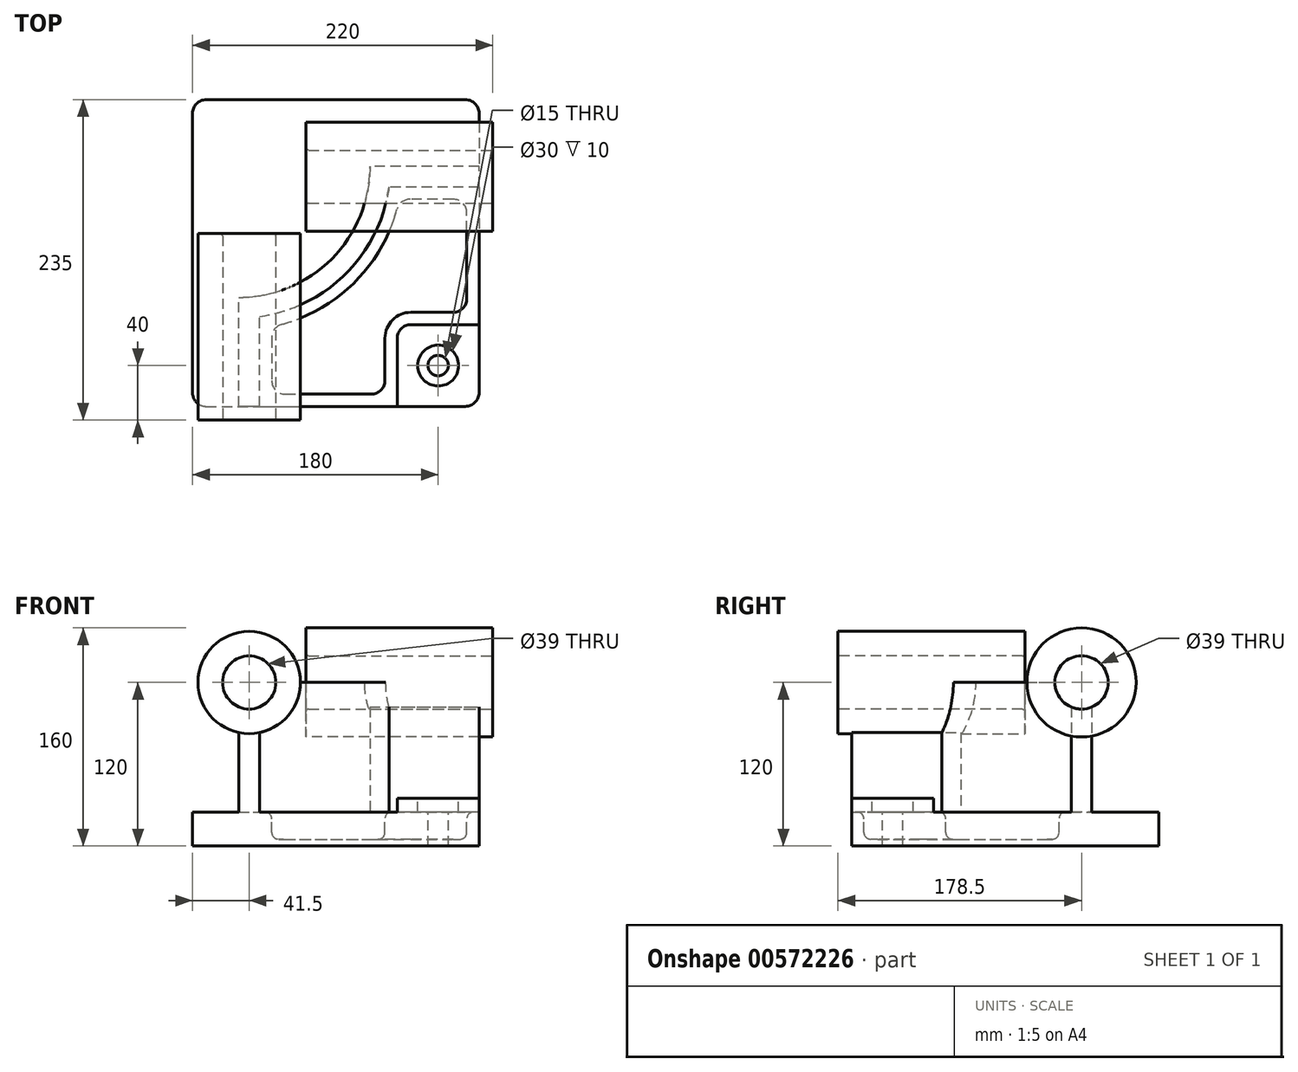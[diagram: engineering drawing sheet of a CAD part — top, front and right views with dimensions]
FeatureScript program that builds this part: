
annotation { "Feature Type Name" : "Feature", "Feature Type Description" : "" }
export const myFeature = defineFeature(function(context is Context, id is Id, definition is map)
    precondition{}
    {
        {
            var Q0;
            Q0=qCreatedBy(makeId("Top.planeOp"),FACE);
            var sketch = newSketch(context, id + "F0", { "sketchPlane" : qUnion([Q0])});
            skLineSegment(sketch, "E0.bottom", {"start": v(-105, 112.5) * mm, "end": v(105, 112.5) * mm});
            skLineSegment(sketch, "E0.top", {"start": v(-105, -112.5) * mm, "end": v(105, -112.5) * mm});
            skLineSegment(sketch, "E0.left", {"start": v(-105, 112.5) * mm, "end": v(-105, -112.5) * mm});
            skLineSegment(sketch, "E0.right", {"start": v(105, 112.5) * mm, "end": v(105, -112.5) * mm});
            skPoint(sketch, "E0.middle", {"position": v(0, 0) * mm});
            skSolve(sketch);
        }
        {
            var Q0;
            Q0=makeQuery(id+"F0.imprint","IMPRINT",FACE,{"disambiguationData":[TD([[makeQuery(id+"F0.imprint","IMPRINT",EDGE,{"derivedFrom":sQuery(id+"F0.wireOp",EDGE,"E0.bottom")}),-1.0]])]});
            extrude(context, id + "F1", {"entities" : qUnion([Q0]), "depth" : 25 * mm});
        }
        {
            var Q0;
            Q0=makeQuery(id+"F1.opExtrude","CAP_FACE",FACE,{"disambiguationData":[OSD([sQuery(id+"F0.wireOp",EDGE,"E0.bottom"),sQuery(id+"F0.wireOp",EDGE,"E0.top"),sQuery(id+"F0.wireOp",EDGE,"E0.left"),sQuery(id+"F0.wireOp",EDGE,"E0.right")])],"isStart":false});
            var sketch = newSketch(context, id + "F2", { "sketchPlane" : qUnion([Q0])});
            skLineSegment(sketch, "E1", {"start": v(-71, -112.5) * mm, "end": v(-71, -32.5) * mm});
            skLineSegment(sketch, "E2", {"start": v(105, 63.5) * mm, "end": v(25, 63.5) * mm});
            skArc(sketch, "E3", {"start": v(-71, -32.5) * mm, "mid": v(-3.11, -4.39) * mm, "end": v(25, 63.5) * mm});
            skLineSegment(sketch, "E4", {"start": v(25, 63.5) * mm, "end": v(-71, 63.5) * mm, "construction": true});
            skLineSegment(sketch, "E5", {"start": v(-71, 63.5) * mm, "end": v(-71, -32.5) * mm, "construction": true});
            skLineSegment(sketch, "E6.0", {"start": v(105, 48.5) * mm, "end": v(38.98, 48.5) * mm});
            skArc(sketch, "E6.1", {"start": v(-56, -46.48) * mm, "mid": v(7.5, -15) * mm, "end": v(38.98, 48.5) * mm});
            skLineSegment(sketch, "E6.2", {"start": v(-56, -112.5) * mm, "end": v(-56, -46.48) * mm});
            skSolve(sketch);
        }
        {
            var Q0;
            {var subQ3=sQuery(id+"F2.wireOp",EDGE,"E1");Q0=makeQuery(id+"F2.imprint","IMPRINT",FACE,{"disambiguationData":[TD([[makeQuery(id+"F2.imprint","IMPRINT",EDGE,{"derivedFrom":subQ3}),-1.0]])]});}
            extrude(context, id + "F3", {"entities" : qUnion([Q0]), "operationType" : NewBodyOperationType.ADD, "depth" : 95 * mm});
        }
        {
            var Q0;
            {var subQ0=sQuery(id+"F0.wireOp",EDGE,"E0.top");Q0=makeQuery(id+"F3.boolean.opBoolean","MERGE",FACE,{"derivedFrom":[makeQuery(id+"F1.opExtrude","SWEPT_FACE",FACE,{"disambiguationData":[OSD([subQ0])]}),makeQuery(id+"F3.opExtrude","SWEPT_FACE",FACE,{"disambiguationData":[OSD([subQ0])]})]});}
            var sketch = newSketch(context, id + "F4", { "sketchPlane" : qUnion([Q0])});
            skCircle(sketch, "E7", {"center": v(-63.5, 120) * mm, "radius": 37.5 * mm});
            skSolve(sketch);
        }
        {
            var Q0;
            {var subQ1=sQuery(id+"F0.wireOp",EDGE,"E0.top");var subQ6=makeQuery(id+"F3.opExtrude","CAP_EDGE",EDGE,{"disambiguationData":[OSD([subQ1])],"isStart":false});Q0=makeQuery(id+"F4.imprint","IMPRINT",FACE,{"disambiguationData":[TD([[makeQuery(id+"F4.imprint","IMPRINT",EDGE,{"derivedFrom":subQ6}),-1.0]])]});}
            var Q1;
            {var subQ1=sQuery(id+"F0.wireOp",EDGE,"E0.top");var subQ6=makeQuery(id+"F3.opExtrude","CAP_EDGE",EDGE,{"disambiguationData":[OSD([subQ1])],"isStart":false});Q1=makeQuery(id+"F4.imprint","IMPRINT",FACE,{"disambiguationData":[TD([[makeQuery(id+"F4.imprint","IMPRINT",EDGE,{"derivedFrom":subQ6}),1.0]])]});}
            var Q2;
            Q2=sQuery(id+"F4.wireOp",EDGE,"E7");
            extrude(context, id + "F5", {"entities" : qUnion([Q0, Q1]), "operationType" : NewBodyOperationType.ADD, "surfaceEntities" : qUnion([Q2]), "depth" : 10 * mm, "hasSecondDirection" : true, "secondDirectionOppositeDirection" : true, "secondDirectionDepth" : 137 * mm - 10 * mm});
        }
        {
            var Q0;
            {var subQ0=sQuery(id+"F0.wireOp",EDGE,"E0.right");Q0=makeQuery(id+"F3.boolean.opBoolean","MERGE",FACE,{"derivedFrom":[makeQuery(id+"F1.opExtrude","SWEPT_FACE",FACE,{"disambiguationData":[OSD([subQ0])]}),makeQuery(id+"F3.opExtrude","SWEPT_FACE",FACE,{"disambiguationData":[OSD([subQ0])]})]});}
            var sketch = newSketch(context, id + "F6", { "sketchPlane" : qUnion([Q0])});
            skCircle(sketch, "E8", {"center": v(56, 120) * mm, "radius": 40 * mm});
            skSolve(sketch);
        }
        {
            var Q0;
            {var subQ1=sQuery(id+"F0.wireOp",EDGE,"E0.right");var subQ6=makeQuery(id+"F3.opExtrude","CAP_EDGE",EDGE,{"disambiguationData":[OSD([subQ1])],"isStart":false});Q0=makeQuery(id+"F6.imprint","IMPRINT",FACE,{"disambiguationData":[TD([[makeQuery(id+"F6.imprint","IMPRINT",EDGE,{"derivedFrom":subQ6}),-1.0]])]});}
            var Q1;
            {var subQ1=sQuery(id+"F0.wireOp",EDGE,"E0.right");var subQ6=makeQuery(id+"F3.opExtrude","CAP_EDGE",EDGE,{"disambiguationData":[OSD([subQ1])],"isStart":false});Q1=makeQuery(id+"F6.imprint","IMPRINT",FACE,{"disambiguationData":[TD([[makeQuery(id+"F6.imprint","IMPRINT",EDGE,{"derivedFrom":subQ6}),1.0]])]});}
            var Q2;
            Q2=sQuery(id+"F6.wireOp",EDGE,"E8");
            extrude(context, id + "F7", {"entities" : qUnion([Q0, Q1]), "surfaceEntities" : qUnion([Q2]), "depth" : 10 * mm, "hasSecondDirection" : true, "secondDirectionOppositeDirection" : true, "secondDirectionDepth" : 127 * mm});
        }
        {
            var Q0;
            {var subQ0=sQuery(id+"F0.wireOp",EDGE,"E0.right");var subQ1=sQuery(id+"F0.wireOp",EDGE,"E0.top");Q0=makeQuery(id+"F3.boolean.opBoolean","SPLIT",FACE,{"disambiguationData":[TD([makeQuery(id+"F3.opExtrude","SWEPT_FACE",FACE,{"disambiguationData":[OSD([sQuery(id+"F2.wireOp",EDGE,"E6.0")])]})])],"derivedFrom":makeQuery(id+"F1.opExtrude","CAP_FACE",FACE,{"disambiguationData":[OSD([sQuery(id+"F0.wireOp",EDGE,"E0.bottom"),subQ1,sQuery(id+"F0.wireOp",EDGE,"E0.left"),subQ0])],"isStart":false})});}
            var sketch = newSketch(context, id + "F8", { "sketchPlane" : qUnion([Q0])});
            skLineSegment(sketch, "E9.bottom", {"start": v(105, -112.5) * mm, "end": v(45, -112.5) * mm});
            skLineSegment(sketch, "E9.top", {"start": v(105, -52.5) * mm, "end": v(45, -52.5) * mm});
            skLineSegment(sketch, "E9.left", {"start": v(105, -112.5) * mm, "end": v(105, -52.5) * mm});
            skLineSegment(sketch, "E9.right", {"start": v(45, -112.5) * mm, "end": v(45, -52.5) * mm});
            skSolve(sketch);
        }
        {
            var Q0;
            Q0=qSketchRegion(id+"F8",true);
            extrude(context, id + "F9", {"entities" : qUnion([Q0]), "operationType" : NewBodyOperationType.ADD, "depth" : 10 * mm});
        }
        {
            var Q0;
            Q0=makeQuery(id+"F9.opExtrude","SWEPT_EDGE",EDGE,{"disambiguationData":[OSD([sQuery(id+"F8.wireOp",EDGE,"E9.top"),sQuery(id+"F8.wireOp",EDGE,"E9.right")])]});
            fillet(context, id + "F10", {"entities" : qUnion([Q0]), "radius" : 10 * mm, "tangentPropagation" : true, "allowEdgeOverflow" : false});
        }
        {
            var Q0;
            {var subQ0=sQuery(id+"F0.wireOp",EDGE,"E0.right");var subQ1=sQuery(id+"F0.wireOp",EDGE,"E0.top");Q0=makeQuery(id+"F3.boolean.opBoolean","SPLIT",FACE,{"disambiguationData":[TD([makeQuery(id+"F3.opExtrude","SWEPT_FACE",FACE,{"disambiguationData":[OSD([sQuery(id+"F2.wireOp",EDGE,"E6.0")])]})])],"derivedFrom":makeQuery(id+"F1.opExtrude","CAP_FACE",FACE,{"disambiguationData":[OSD([sQuery(id+"F0.wireOp",EDGE,"E0.bottom"),subQ1,sQuery(id+"F0.wireOp",EDGE,"E0.left"),subQ0])],"isStart":false})});}
            var sketch = newSketch(context, id + "F11", { "sketchPlane" : qUnion([Q0])});
            skLineSegment(sketch, "E10.0", {"start": v(-47, -54.08) * mm, "end": v(-47, -103.5) * mm});
            skArc(sketch, "E10.1", {"start": v(46.58, 39.5) * mm, "mid": v(13.86, -21.36) * mm, "end": v(-47, -54.08) * mm});
            skLineSegment(sketch, "E10.2", {"start": v(-47, -103.5) * mm, "end": v(36, -103.5) * mm});
            skLineSegment(sketch, "E10.3", {"start": v(96, 39.5) * mm, "end": v(46.58, 39.5) * mm});
            skLineSegment(sketch, "E10.4", {"start": v(36, -103.5) * mm, "end": v(36, -62.5) * mm});
            skArc(sketch, "E10.5", {"start": v(36, -62.5) * mm, "mid": v(41.56, -49.06) * mm, "end": v(55, -43.5) * mm});
            skLineSegment(sketch, "E10.6", {"start": v(55, -43.5) * mm, "end": v(96, -43.5) * mm});
            skLineSegment(sketch, "E10.7", {"start": v(96, -43.5) * mm, "end": v(96, 39.5) * mm});
            skSolve(sketch);
        }
        {
            var Q0;
            Q0=makeQuery(id+"F11.imprint","IMPRINT",FACE,{"disambiguationData":[TD([[makeQuery(id+"F11.imprint","IMPRINT",EDGE,{"derivedFrom":sQuery(id+"F11.wireOp",EDGE,"E10.0")}),1.0]])]});
            extrude(context, id + "F12", {"entities" : qUnion([Q0]), "operationType" : NewBodyOperationType.REMOVE, "oppositeDirection" : true, "depth" : 20 * mm});
        }
        {
            var Q0;
            Q0=makeQuery(id+"F9.opExtrude","CAP_FACE",FACE,{"disambiguationData":[OSD([sQuery(id+"F8.wireOp",EDGE,"E9.bottom"),sQuery(id+"F8.wireOp",EDGE,"E9.top"),sQuery(id+"F8.wireOp",EDGE,"E9.left"),sQuery(id+"F8.wireOp",EDGE,"E9.right")])],"isStart":false});
            var sketch = newSketch(context, id + "F13", { "sketchPlane" : qUnion([Q0])});
            skCircle(sketch, "E11", {"center": v(75, -82.5) * mm, "radius": 15 * mm});
            skSolve(sketch);
        }
        {
            var Q0;
            Q0=sQuery(id+"F13.wireOp",VERTEX,"E11.center");
            var Q1;
            Q1=makeQuery(id+"F1.opExtrude","SWEPT_BODY",BODY,{"disambiguationData":[OSD([sQuery(id+"F0.wireOp",EDGE,"E0.bottom"),sQuery(id+"F0.wireOp",EDGE,"E0.top"),sQuery(id+"F0.wireOp",EDGE,"E0.left"),sQuery(id+"F0.wireOp",EDGE,"E0.right")])]});
            hole(context, id + "F14", {"style" : HoleStyle.C_BORE, "endStyle" : HoleEndStyle.THROUGH, "holeDiameter" : 15 * mm, "cBoreDiameter" : 30 * mm, "cBoreDepth" : 10 * mm, "isTappedThrough" : true, "tappedDepth" : 12.7 * mm, "tapClearance" : 3, "locations" : qUnion([Q0]), "scope" : qUnion([Q1])});
        }
        {
            var Q0;
            Q0=makeQuery(id+"F12.boolean.opBoolean","COPY",EDGE,{"derivedFrom":makeQuery(id+"F12.opExtrude","SWEPT_EDGE",EDGE,{"disambiguationData":[OSD([sQuery(id+"F11.wireOp",EDGE,"E10.0"),sQuery(id+"F11.wireOp",EDGE,"E10.1")])]})});
            var Q1;
            Q1=makeQuery(id+"F12.boolean.opBoolean","COPY",EDGE,{"derivedFrom":makeQuery(id+"F12.opExtrude","SWEPT_EDGE",EDGE,{"disambiguationData":[OSD([sQuery(id+"F11.wireOp",EDGE,"E10.1"),sQuery(id+"F11.wireOp",EDGE,"E10.3")])]})});
            var Q2;
            Q2=makeQuery(id+"F12.boolean.opBoolean","COPY",EDGE,{"derivedFrom":makeQuery(id+"F12.opExtrude","SWEPT_EDGE",EDGE,{"disambiguationData":[OSD([sQuery(id+"F11.wireOp",EDGE,"E10.3"),sQuery(id+"F11.wireOp",EDGE,"E10.7")])]})});
            var Q3;
            Q3=makeQuery(id+"F12.boolean.opBoolean","COPY",EDGE,{"derivedFrom":makeQuery(id+"F12.opExtrude","SWEPT_EDGE",EDGE,{"disambiguationData":[OSD([sQuery(id+"F11.wireOp",EDGE,"E10.6"),sQuery(id+"F11.wireOp",EDGE,"E10.7")])]})});
            var Q4;
            Q4=makeQuery(id+"F12.boolean.opBoolean","COPY",EDGE,{"derivedFrom":makeQuery(id+"F12.opExtrude","SWEPT_EDGE",EDGE,{"disambiguationData":[OSD([sQuery(id+"F11.wireOp",EDGE,"E10.2"),sQuery(id+"F11.wireOp",EDGE,"E10.4")])]})});
            var Q5;
            Q5=makeQuery(id+"F12.boolean.opBoolean","COPY",EDGE,{"derivedFrom":makeQuery(id+"F12.opExtrude","SWEPT_EDGE",EDGE,{"disambiguationData":[OSD([sQuery(id+"F11.wireOp",EDGE,"E10.0"),sQuery(id+"F11.wireOp",EDGE,"E10.2")])]})});
            fillet(context, id + "F15", {"entities" : qUnion([Q0, Q1, Q2, Q3, Q4, Q5]), "radius" : 10 * mm, "tangentPropagation" : true, "allowEdgeOverflow" : false});
        }
        {
            var Q0;
            Q0=makeQuery(id+"F5.opExtrude","CAP_FACE",FACE,{"disambiguationData":[OSD([sQuery(id+"F4.wireOp",EDGE,"E7")])],"isStart":false});
            var sketch = newSketch(context, id + "F16", { "sketchPlane" : qUnion([Q0])});
            skCircle(sketch, "E12", {"center": v(-63.5, 120) * mm, "radius": 19.5 * mm});
            skSolve(sketch);
        }
        {
            var Q0;
            Q0=makeQuery(id+"F7.opExtrude","CAP_FACE",FACE,{"disambiguationData":[OSD([sQuery(id+"F6.wireOp",EDGE,"E8")])],"isStart":false});
            var sketch = newSketch(context, id + "F17", { "sketchPlane" : qUnion([Q0])});
            skCircle(sketch, "E13", {"center": v(56, 120) * mm, "radius": 19.5 * mm});
            skSolve(sketch);
        }
        {
            var Q0;
            Q0=qSketchRegion(id+"F16",true);
            extrude(context, id + "F18", {"entities" : qUnion([Q0]), "operationType" : NewBodyOperationType.REMOVE, "endBound" : BoundingType.THROUGH_ALL, "oppositeDirection" : true, "depth" : 25.4 * mm});
        }
        {
            var Q0;
            Q0=makeQuery(id+"F17.imprint","IMPRINT",FACE,{"disambiguationData":[TD([[makeQuery(id+"F17.imprint","IMPRINT",EDGE,{"derivedFrom":sQuery(id+"F17.wireOp",EDGE,"E13")}),1.0]])]});
            extrude(context, id + "F19", {"entities" : qUnion([Q0]), "operationType" : NewBodyOperationType.REMOVE, "endBound" : BoundingType.THROUGH_ALL, "oppositeDirection" : true, "depth" : 25.4 * mm});
        }
        {
            var Q0;
            Q0=makeQuery(id+"F18.boolean.opBoolean","COPY",EDGE,{"derivedFrom":makeQuery(id+"F18.opExtrude","CAP_EDGE",EDGE,{"disambiguationData":[OSD([sQuery(id+"F16.wireOp",EDGE,"E12")])],"isStart":true})});
            var Q1;
            Q1=makeQuery(id+"F19.boolean.opBoolean","COPY",EDGE,{"derivedFrom":makeQuery(id+"F19.opExtrude","CAP_EDGE",EDGE,{"disambiguationData":[OSD([sQuery(id+"F17.wireOp",EDGE,"E13")])],"isStart":true})});
            var Q2;
            Q2=makeQuery(id+"F19.boolean.opBoolean","INTERSECT",EDGE,{"derivedFrom":[makeQuery(id+"F7.opExtrude","CAP_FACE",FACE,{"disambiguationData":[OSD([sQuery(id+"F6.wireOp",EDGE,"E8")])],"isStart":true}),makeQuery(id+"F19.opExtrude","SWEPT_FACE",FACE,{"disambiguationData":[OSD([sQuery(id+"F17.wireOp",EDGE,"E13")])]})]});
            var Q3;
            Q3=makeQuery(id+"F18.boolean.opBoolean","INTERSECT",EDGE,{"derivedFrom":[makeQuery(id+"F5.opExtrude","CAP_FACE",FACE,{"disambiguationData":[OSD([sQuery(id+"F4.wireOp",EDGE,"E7")])],"isStart":true}),makeQuery(id+"F18.opExtrude","SWEPT_FACE",FACE,{"disambiguationData":[OSD([sQuery(id+"F16.wireOp",EDGE,"E12")])]})]});
            fillet(context, id + "F20", {"entities" : qUnion([Q0, Q1, Q2, Q3]), "radius" : 2 * mm, "tangentPropagation" : true, "allowEdgeOverflow" : false});
        }
        {
            var Q0;
            Q0=makeQuery(id+"F9.boolean.opBoolean","MERGE",EDGE,{"derivedFrom":[makeQuery(id+"F1.opExtrude","SWEPT_EDGE",EDGE,{"disambiguationData":[OSD([sQuery(id+"F0.wireOp",EDGE,"E0.top"),sQuery(id+"F0.wireOp",EDGE,"E0.right")])]}),makeQuery(id+"F9.opExtrude","SWEPT_EDGE",EDGE,{"disambiguationData":[OSD([sQuery(id+"F8.wireOp",EDGE,"E9.bottom"),sQuery(id+"F8.wireOp",EDGE,"E9.left")])]})]});
            var Q1;
            Q1=makeQuery(id+"F1.opExtrude","SWEPT_EDGE",EDGE,{"disambiguationData":[OSD([sQuery(id+"F0.wireOp",EDGE,"E0.top"),sQuery(id+"F0.wireOp",EDGE,"E0.left")])]});
            var Q2;
            Q2=makeQuery(id+"F1.opExtrude","SWEPT_EDGE",EDGE,{"disambiguationData":[OSD([sQuery(id+"F0.wireOp",EDGE,"E0.bottom"),sQuery(id+"F0.wireOp",EDGE,"E0.right")])]});
            var Q3;
            Q3=makeQuery(id+"F1.opExtrude","SWEPT_EDGE",EDGE,{"disambiguationData":[OSD([sQuery(id+"F0.wireOp",EDGE,"E0.bottom"),sQuery(id+"F0.wireOp",EDGE,"E0.left")])]});
            fillet(context, id + "F21", {"entities" : qUnion([Q0, Q1, Q2, Q3]), "radius" : 10 * mm, "tangentPropagation" : true, "allowEdgeOverflow" : false});
        }
        {
            var Q0;
            Q0=makeQuery(id+"F12.boolean.opBoolean","COPY",EDGE,{"derivedFrom":makeQuery(id+"F12.opExtrude","CAP_EDGE",EDGE,{"disambiguationData":[OSD([sQuery(id+"F11.wireOp",EDGE,"E10.0")])],"isStart":true})});
            var Q1;
            {var subQ0=sQuery(id+"F0.wireOp",EDGE,"E0.right");var subQ1=sQuery(id+"F0.wireOp",EDGE,"E0.top");Q1=makeQuery(id+"F15.opFillet","BLEND_EDGE",EDGE,{"blendedFrom":[makeQuery(id+"F12.boolean.opBoolean","COPY",EDGE,{"derivedFrom":makeQuery(id+"F12.opExtrude","SWEPT_EDGE",EDGE,{"disambiguationData":[OSD([sQuery(id+"F11.wireOp",EDGE,"E10.0"),sQuery(id+"F11.wireOp",EDGE,"E10.1")])]})}),makeQuery(id+"F3.boolean.opBoolean","SPLIT",FACE,{"disambiguationData":[TD([makeQuery(id+"F3.opExtrude","SWEPT_FACE",FACE,{"disambiguationData":[OSD([sQuery(id+"F2.wireOp",EDGE,"E6.0")])]})])],"derivedFrom":makeQuery(id+"F1.opExtrude","CAP_FACE",FACE,{"disambiguationData":[OSD([sQuery(id+"F0.wireOp",EDGE,"E0.bottom"),subQ1,sQuery(id+"F0.wireOp",EDGE,"E0.left"),subQ0])],"isStart":false})})],"blendedInto":[makeQuery(id+"F3.boolean.opBoolean","SPLIT",FACE,{"disambiguationData":[TD([makeQuery(id+"F3.opExtrude","SWEPT_FACE",FACE,{"disambiguationData":[OSD([sQuery(id+"F2.wireOp",EDGE,"E6.0")])]})])],"derivedFrom":makeQuery(id+"F1.opExtrude","CAP_FACE",FACE,{"disambiguationData":[OSD([sQuery(id+"F0.wireOp",EDGE,"E0.bottom"),subQ1,sQuery(id+"F0.wireOp",EDGE,"E0.left"),subQ0])],"isStart":false})})]});}
            var Q2;
            Q2=makeQuery(id+"F12.boolean.opBoolean","COPY",EDGE,{"derivedFrom":makeQuery(id+"F12.opExtrude","CAP_EDGE",EDGE,{"disambiguationData":[OSD([sQuery(id+"F11.wireOp",EDGE,"E10.0")])],"isStart":false})});
            var Q3;
            {var subQ0=sQuery(id+"F11.wireOp",EDGE,"E10.1");var subQ1=sQuery(id+"F11.wireOp",EDGE,"E10.0");Q3=makeQuery(id+"F15.opFillet","BLEND_EDGE",EDGE,{"blendedFrom":[makeQuery(id+"F12.boolean.opBoolean","COPY",EDGE,{"derivedFrom":makeQuery(id+"F12.opExtrude","SWEPT_EDGE",EDGE,{"disambiguationData":[OSD([subQ1,subQ0])]})}),makeQuery(id+"F12.boolean.opBoolean","COPY",FACE,{"derivedFrom":makeQuery(id+"F12.opExtrude","CAP_FACE",FACE,{"disambiguationData":[OSD([subQ1,subQ0,sQuery(id+"F11.wireOp",EDGE,"E10.2"),sQuery(id+"F11.wireOp",EDGE,"E10.3"),sQuery(id+"F11.wireOp",EDGE,"E10.4"),sQuery(id+"F11.wireOp",EDGE,"E10.5"),sQuery(id+"F11.wireOp",EDGE,"E10.6"),sQuery(id+"F11.wireOp",EDGE,"E10.7")])],"isStart":false})})],"blendedInto":[makeQuery(id+"F12.boolean.opBoolean","COPY",FACE,{"derivedFrom":makeQuery(id+"F12.opExtrude","CAP_FACE",FACE,{"disambiguationData":[OSD([subQ1,subQ0,sQuery(id+"F11.wireOp",EDGE,"E10.2"),sQuery(id+"F11.wireOp",EDGE,"E10.3"),sQuery(id+"F11.wireOp",EDGE,"E10.4"),sQuery(id+"F11.wireOp",EDGE,"E10.5"),sQuery(id+"F11.wireOp",EDGE,"E10.6"),sQuery(id+"F11.wireOp",EDGE,"E10.7")])],"isStart":false})})]});}
            var Q4;
            Q4=makeQuery(id+"F12.boolean.opBoolean","COPY",EDGE,{"derivedFrom":makeQuery(id+"F12.opExtrude","CAP_EDGE",EDGE,{"disambiguationData":[OSD([sQuery(id+"F11.wireOp",EDGE,"E10.1")])],"isStart":false})});
            fillet(context, id + "F22", {"entities" : qUnion([Q0, Q1, Q2, Q3, Q4]), "radius" : 5.08 * mm, "tangentPropagation" : true, "allowEdgeOverflow" : false});
        }
    });
